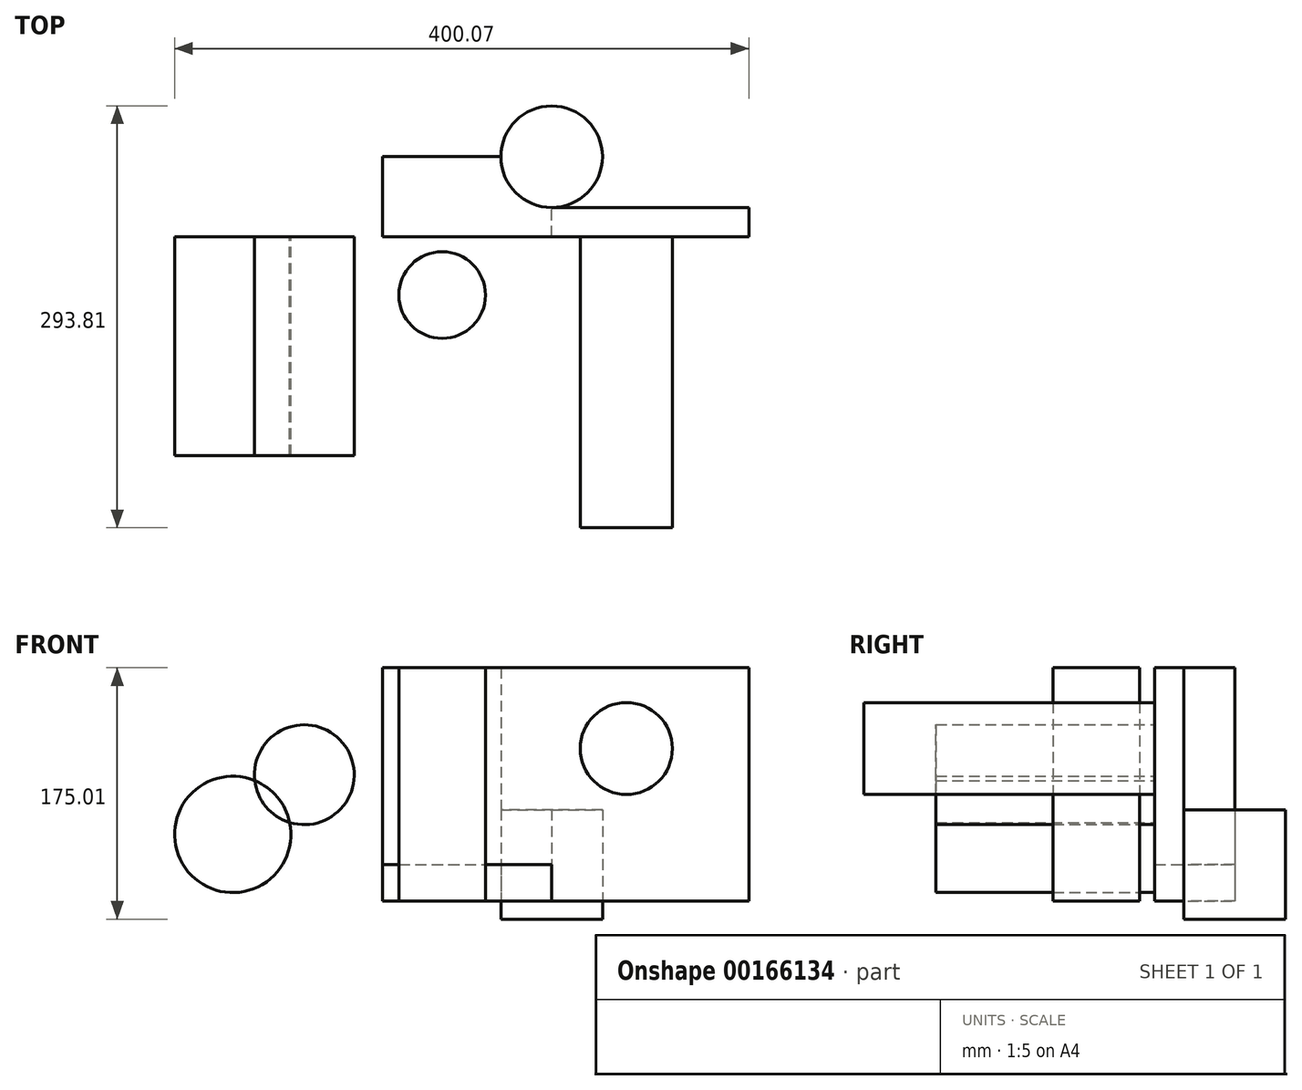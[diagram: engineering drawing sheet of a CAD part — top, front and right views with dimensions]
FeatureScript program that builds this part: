
annotation { "Feature Type Name" : "Feature", "Feature Type Description" : "" }
export const myFeature = defineFeature(function(context is Context, id is Id, definition is map)
    precondition{}
    {
        {
            var Q0;
            Q0=qCreatedBy(makeId("Top.planeOp"),FACE);
            var sketch = newSketch(context, id + "F0", { "sketchPlane" : qUnion([Q0])});
            skLineSegment(sketch, "E0.bottom", {"start": v(0, 0) * mm, "end": v(117.68, 0) * mm});
            skLineSegment(sketch, "E0.top", {"start": v(0, 55.72) * mm, "end": v(117.68, 55.72) * mm});
            skLineSegment(sketch, "E0.left", {"start": v(0, 0) * mm, "end": v(0, 55.72) * mm});
            skLineSegment(sketch, "E0.right", {"start": v(117.68, 0) * mm, "end": v(117.68, 55.72) * mm});
            skCircle(sketch, "E1", {"center": v(117.68, 55.72) * mm, "radius": 35.4 * mm});
            skSolve(sketch);
        }
        {
            var Q0;
            {var subQ0=sQuery(id+"F0.wireOp",EDGE,"E0.right");var subQ1=sQuery(id+"F0.wireOp",EDGE,"E0.top");var subQ2=makeQuery(id+"F0.imprint","INTERSECT",VERTEX,{"derivedFrom":[subQ1,subQ0]});Q0=makeQuery(id+"F0.imprint","IMPRINT",FACE,{"disambiguationData":[TD([[makeQuery(id+"F0.imprint","IMPRINT",EDGE,{"disambiguationData":[TD([[subQ2,1.0]])],"derivedFrom":subQ1}),1.0]])]});}
            var Q1;
            {var subQ0=sQuery(id+"F0.wireOp",EDGE,"E0.right");var subQ1=sQuery(id+"F0.wireOp",EDGE,"E0.top");var subQ2=makeQuery(id+"F0.imprint","INTERSECT",VERTEX,{"derivedFrom":[subQ1,subQ0]});Q1=makeQuery(id+"F0.imprint","IMPRINT",FACE,{"disambiguationData":[TD([[makeQuery(id+"F0.imprint","IMPRINT",EDGE,{"disambiguationData":[TD([[subQ2,1.0]])],"derivedFrom":subQ1}),-1.0]])]});}
            extrude(context, id + "F1", {"entities" : qUnion([Q0, Q1]), "endBound" : BoundingType.SYMMETRIC, "depth" : 25.4 * mm});
        }
        {
            var Q0;
            Q0 = qSketchRegion(id + "F0", true);
            var Q1;
            Q1=makeQuery(id+"F1.opExtrude","CAP_FACE",FACE,{"disambiguationData":[OSD([sQuery(id+"F0.wireOp",EDGE,"E1")])],"isStart":false});
            extrude(context, id + "F2", {"entities" : qUnion([Q0, Q1]), "operationType" : NewBodyOperationType.ADD, "depth" : 50.8 * mm});
        }
        {
            var Q0;
            Q0=makeQuery(id+"F2.opExtrude","SWEPT_FACE",FACE,{"disambiguationData":[OSD([sQuery(id+"F0.wireOp",EDGE,"E0.right")])]});
            extrude(context, id + "F3", {"entities" : qUnion([Q0]), "operationType" : NewBodyOperationType.ADD, "depth" : 137.4 * mm});
        }
        {
            var Q0;
            Q0=qCreatedBy(makeId("Front.planeOp"),FACE);
            var sketch = newSketch(context, id + "F4", { "sketchPlane" : qUnion([Q0])});
            skCircle(sketch, "E2", {"center": v(-104.46, 46.3) * mm, "radius": 40.51 * mm});
            skCircle(sketch, "E3", {"center": v(-54.6, 87.84) * mm, "radius": 34.77 * mm});
            skSolve(sketch);
        }
        {
            var Q0;
            {var subQ0=sQuery(id+"F4.wireOp",EDGE,"E3");var subQ1=sQuery(id+"F4.wireOp",EDGE,"E2");var subQ2=makeQuery(id+"F4.imprint","INTERSECT",VERTEX,{"disambiguationData":[OD(0.0)],"derivedFrom":[subQ1,subQ0]});Q0=makeQuery(id+"F4.imprint","IMPRINT",FACE,{"disambiguationData":[TD([[makeQuery(id+"F4.imprint","IMPRINT",EDGE,{"disambiguationData":[TD([[subQ2,1.0]])],"derivedFrom":subQ1}),-1.0]])]});}
            var Q1;
            {var subQ0=sQuery(id+"F4.wireOp",EDGE,"E3");var subQ1=sQuery(id+"F4.wireOp",EDGE,"E2");var subQ2=makeQuery(id+"F4.imprint","INTERSECT",VERTEX,{"disambiguationData":[OD(0.0)],"derivedFrom":[subQ1,subQ0]});Q1=makeQuery(id+"F4.imprint","IMPRINT",FACE,{"disambiguationData":[TD([[makeQuery(id+"F4.imprint","IMPRINT",EDGE,{"disambiguationData":[TD([[subQ2,-1.0]])],"derivedFrom":subQ1}),1.0]])]});}
            extrude(context, id + "F5", {"entities" : qUnion([Q0, Q1]), "depth" : 152.4 * mm});
        }
        {
            var Q0;
            Q0=qCreatedBy(makeId("Top.planeOp"),FACE);
            var sketch = newSketch(context, id + "F6", { "sketchPlane" : qUnion([Q0])});
            skCircle(sketch, "E4", {"center": v(41.45, -40.63) * mm, "radius": 30.19 * mm});
            skSolve(sketch);
        }
        {
            var Q0;
            Q0=makeQuery(id+"F6.imprint","IMPRINT",FACE,{"disambiguationData":[TD([[makeQuery(id+"F6.imprint","IMPRINT",EDGE,{"derivedFrom":sQuery(id+"F6.wireOp",EDGE,"E4")}),1.0]])]});
            var Q1;
            {var subQ0=sQuery(id+"F0.wireOp",EDGE,"E0.right");Q1=makeQuery(id+"F3.boolean.opBoolean","MERGE",FACE,{"derivedFrom":[makeQuery(id+"F2.opExtrude","CAP_FACE",FACE,{"disambiguationData":[OSD([sQuery(id+"F0.wireOp",EDGE,"E0.bottom"),sQuery(id+"F0.wireOp",EDGE,"E0.top"),sQuery(id+"F0.wireOp",EDGE,"E0.left"),subQ0,sQuery(id+"F0.wireOp",EDGE,"E1")])],"isStart":false}),makeQuery(id+"F3.opExtrude","SWEPT_FACE",FACE,{"disambiguationData":[OSD([subQ0]),TDD([makeQuery(id+"F2.opExtrude","CAP_EDGE",EDGE,{"disambiguationData":[OSD([subQ0])],"isStart":false})])]})]});}
            extrude(context, id + "F7", {"entities" : qUnion([Q0, Q1]), "operationType" : NewBodyOperationType.ADD, "depth" : 111.5 * mm});
        }
        {
            var Q0;
            Q0=makeQuery(id+"F7.opExtrude","CAP_FACE",FACE,{"disambiguationData":[OSD([sQuery(id+"F6.wireOp",EDGE,"E4")])],"isStart":false});
            var Q1;
            Q1=makeQuery(id+"F7.opExtrude","CAP_FACE",FACE,{"disambiguationData":[OSD([sQuery(id+"F0.wireOp",EDGE,"E0.bottom"),sQuery(id+"F0.wireOp",EDGE,"E0.top"),sQuery(id+"F0.wireOp",EDGE,"E0.left"),sQuery(id+"F0.wireOp",EDGE,"E0.right"),sQuery(id+"F0.wireOp",EDGE,"E1")])],"isStart":false});
            extrude(context, id + "F8", {"entities" : qUnion([Q0]), "operationType" : NewBodyOperationType.ADD, "endBound" : BoundingType.UP_TO_SURFACE, "endBoundEntityFace" : qUnion([Q1]), "depth" : 61.98 * mm});
        }
        {
            var Q0;
            {var subQ0=sQuery(id+"F0.wireOp",EDGE,"E0.right");var subQ1=sQuery(id+"F0.wireOp",EDGE,"E0.bottom");Q0=makeQuery(id+"F7.boolean.opBoolean","MERGE",FACE,{"derivedFrom":[makeQuery(id+"F3.boolean.opBoolean","MERGE",FACE,{"derivedFrom":[makeQuery(id+"F2.opExtrude","SWEPT_FACE",FACE,{"disambiguationData":[OSD([subQ1])]}),makeQuery(id+"F3.opExtrude","SWEPT_FACE",FACE,{"disambiguationData":[OSD([subQ1,subQ0])]})]}),makeQuery(id+"F7.opExtrude","SWEPT_FACE",FACE,{"disambiguationData":[OSD([subQ1,subQ0])]})]});}
            var sketch = newSketch(context, id + "F9", { "sketchPlane" : qUnion([Q0])});
            skCircle(sketch, "E5", {"center": v(169.72, 106.08) * mm, "radius": 32.04 * mm});
            skSolve(sketch);
        }
        {
            var Q0;
            Q0=makeQuery(id+"F9.imprint","IMPRINT",FACE,{"disambiguationData":[TD([[makeQuery(id+"F9.imprint","IMPRINT",EDGE,{"derivedFrom":sQuery(id+"F9.wireOp",EDGE,"E5")}),1.0]])]});
            extrude(context, id + "F10", {"entities" : qUnion([Q0]), "operationType" : NewBodyOperationType.ADD, "depth" : 202.7 * mm});
        }
        {
            var Q0;
            {var subQ1=sQuery(id+"F0.wireOp",EDGE,"E0.bottom");Q0=makeQuery(id+"F0.imprint","IMPRINT",FACE,{"disambiguationData":[TD([[makeQuery(id+"F0.imprint","IMPRINT",EDGE,{"derivedFrom":subQ1}),1.0]])]});}
            extrude(context, id + "F11", {"entities" : qUnion([Q0]), "depth" : 25.4 * mm});
        }
    });
